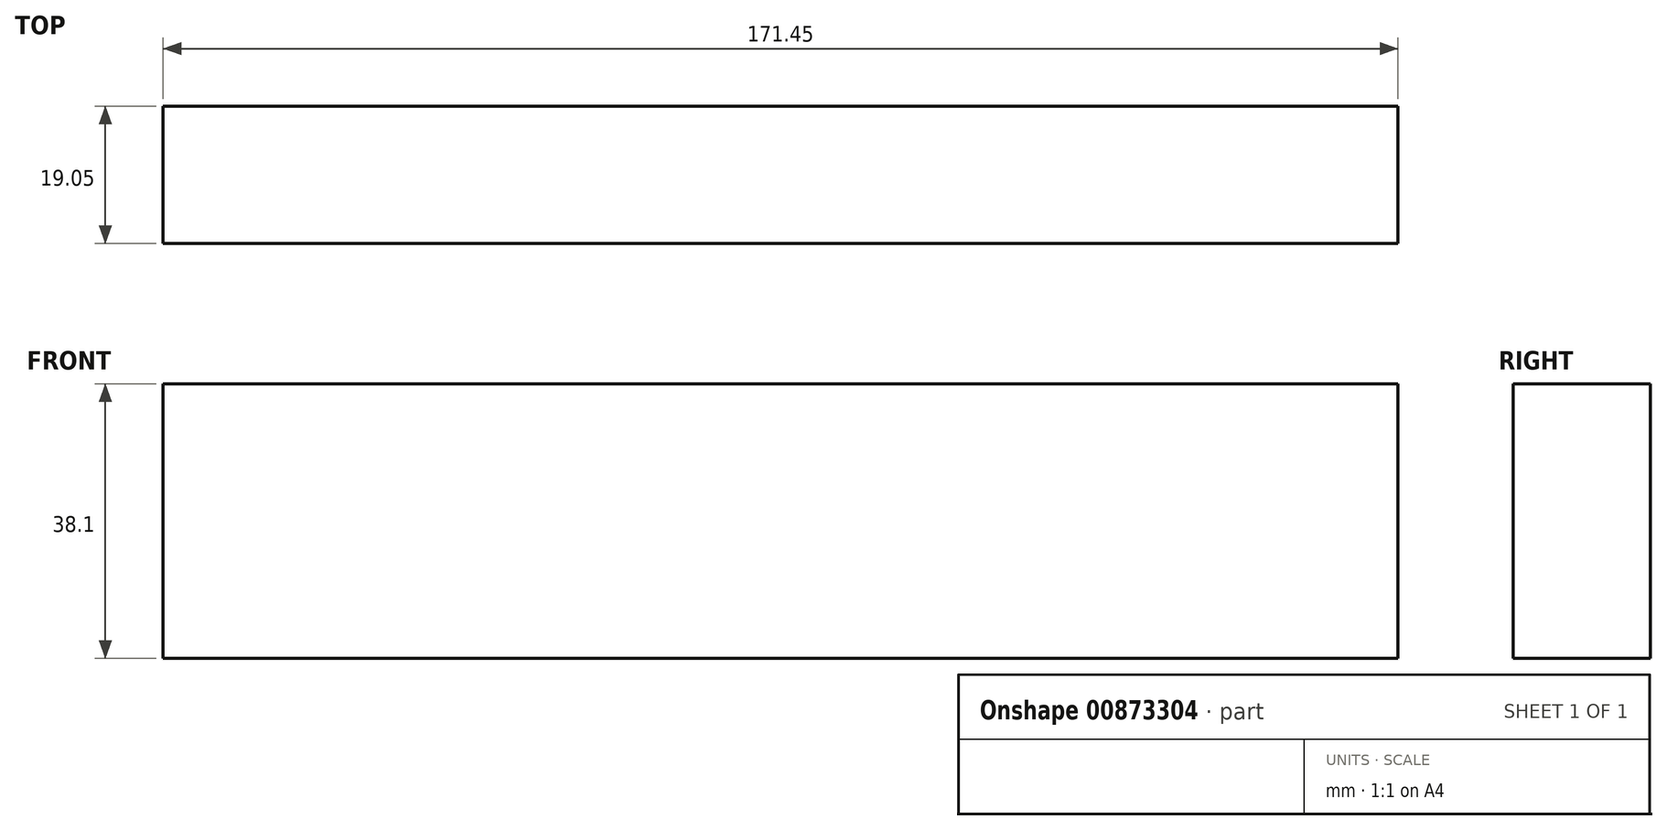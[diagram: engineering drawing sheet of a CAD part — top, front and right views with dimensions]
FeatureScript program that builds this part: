
annotation { "Feature Type Name" : "Feature", "Feature Type Description" : "" }
export const myFeature = defineFeature(function(context is Context, id is Id, definition is map)
    precondition{}
    {
        {
            var Q0;
            Q0=qCreatedBy(makeId("Front.planeOp"),FACE);
            var sketch = newSketch(context, id + "F0", { "sketchPlane" : qUnion([Q0])});
            skLineSegment(sketch, "E0.bottom", {"start": v(0, 0) * mm, "end": v(-171.45, 0) * mm});
            skLineSegment(sketch, "E0.top", {"start": v(0, 38.1) * mm, "end": v(-171.45, 38.1) * mm});
            skLineSegment(sketch, "E0.left", {"start": v(0, 0) * mm, "end": v(0, 38.1) * mm});
            skLineSegment(sketch, "E0.right", {"start": v(-171.45, 0) * mm, "end": v(-171.45, 38.1) * mm});
            skSolve(sketch);
        }
        {
            var Q0;
            Q0=qSketchRegion(id+"F0",true);
            extrude(context, id + "F1", {"entities" : qUnion([Q0]), "depth" : 19.05 * mm, "offsetDistance" : 25.4 * mm});
        }
    });
